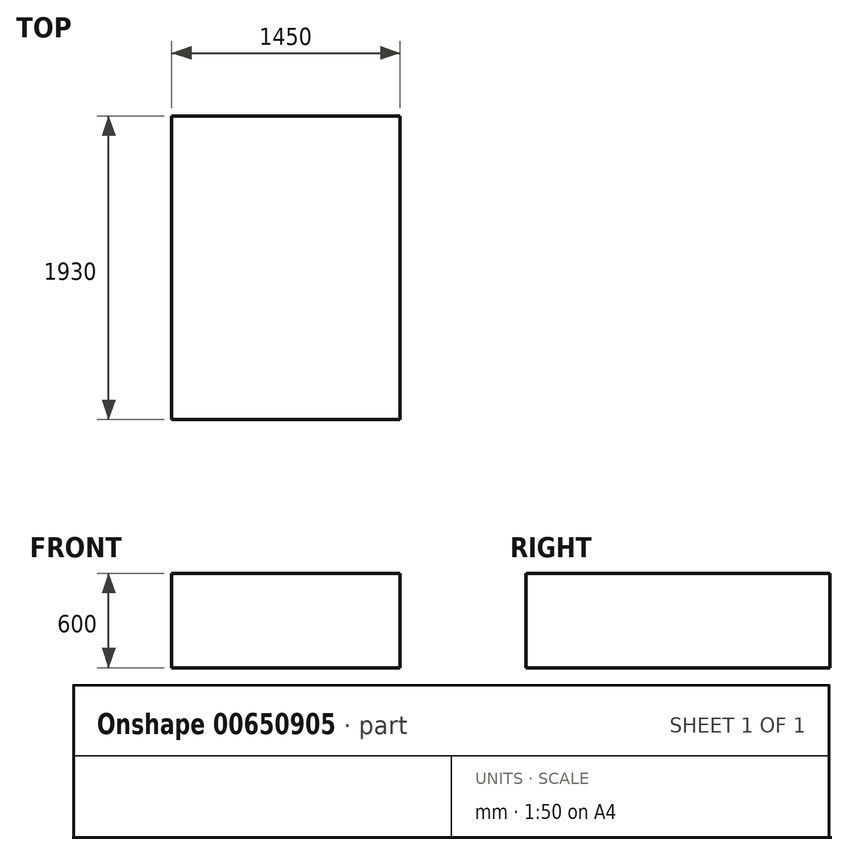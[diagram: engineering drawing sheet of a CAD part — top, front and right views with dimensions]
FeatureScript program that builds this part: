
annotation { "Feature Type Name" : "Feature", "Feature Type Description" : "" }
export const myFeature = defineFeature(function(context is Context, id is Id, definition is map)
    precondition{}
    {
        {
            var Q0;
            Q0=qCreatedBy(makeId("Top.planeOp"),FACE);
            var sketch = newSketch(context, id + "F0", { "sketchPlane" : qUnion([Q0])});
            skLineSegment(sketch, "E0.bottom", {"start": v(-1053.55, 970.1) * mm, "end": v(396.45, 970.1) * mm});
            skLineSegment(sketch, "E0.top", {"start": v(-1053.55, -959.9) * mm, "end": v(396.45, -959.9) * mm});
            skLineSegment(sketch, "E0.left", {"start": v(-1053.55, 970.1) * mm, "end": v(-1053.55, -959.9) * mm});
            skLineSegment(sketch, "E0.right", {"start": v(396.45, 970.1) * mm, "end": v(396.45, -959.9) * mm});
            skSolve(sketch);
        }
        {
            var Q0;
            Q0=makeQuery(id+"F0.imprint","IMPRINT",FACE,{"disambiguationData":[TD([[makeQuery(id+"F0.imprint","IMPRINT",EDGE,{"derivedFrom":sQuery(id+"F0.wireOp",EDGE,"E0.bottom")}),-1.0]])]});
            extrude(context, id + "F1", {"entities" : qUnion([Q0]), "depth" : 600 * mm, "offsetDistance" : 25 * mm});
        }
    });
